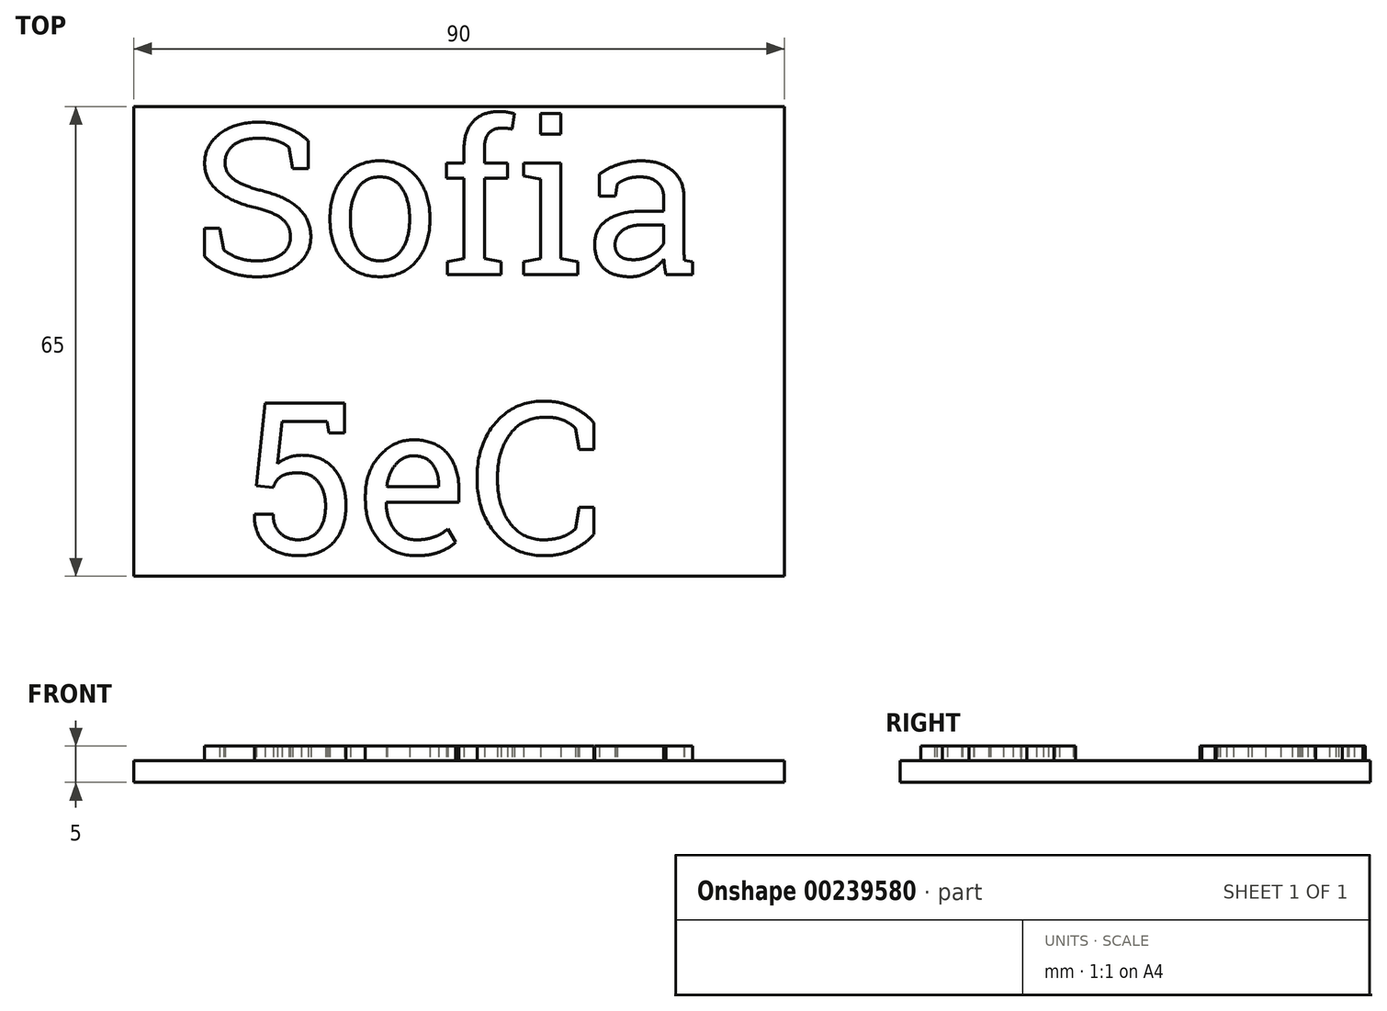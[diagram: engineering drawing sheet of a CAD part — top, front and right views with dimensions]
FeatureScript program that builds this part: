
annotation { "Feature Type Name" : "Feature", "Feature Type Description" : "" }
export const myFeature = defineFeature(function(context is Context, id is Id, definition is map)
    precondition{}
    {
        {
            var Q0;
            Q0=qCreatedBy(makeId("Top.planeOp"),FACE);
            var sketch = newSketch(context, id + "F0", { "sketchPlane" : qUnion([Q0])});
            skLineSegment(sketch, "E0.bottom", {"start": v(0, 0) * mm, "end": v(90, 0) * mm});
            skLineSegment(sketch, "E0.top", {"start": v(0, -65) * mm, "end": v(90, -65) * mm});
            skLineSegment(sketch, "E0.left", {"start": v(0, 0) * mm, "end": v(0, -65) * mm});
            skLineSegment(sketch, "E0.right", {"start": v(90, 0) * mm, "end": v(90, -65) * mm});
            skSolve(sketch);
        }
        {
            var Q0;
            Q0=makeQuery(id+"F0.imprint","IMPRINT",FACE,{"disambiguationData":[TD([[makeQuery(id+"F0.imprint","IMPRINT",EDGE,{"derivedFrom":sQuery(id+"F0.wireOp",EDGE,"E0.bottom")}),-1.0]])]});
            extrude(context, id + "F1", {"entities" : qUnion([Q0]), "depth" : 3 * mm});
        }
        {
            var Q0;
            Q0=makeQuery(id+"F1.opExtrude","CAP_FACE",FACE,{"disambiguationData":[OSD([sQuery(id+"F0.wireOp",EDGE,"E0.bottom"),sQuery(id+"F0.wireOp",EDGE,"E0.top"),sQuery(id+"F0.wireOp",EDGE,"E0.left"),sQuery(id+"F0.wireOp",EDGE,"E0.right")])],"isStart":false});
            var sketch = newSketch(context, id + "F2", { "sketchPlane" : qUnion([Q0])});
            skText(sketch, "E1", { "text": "Sofia \n 5eC", "fontName": "RobotoSlab-Regular.ttf"});
            const initialGuessF2  = {"E1": [0.00807, -0.02326, 1, 0, 0.02105]};
            skSetInitialGuess(sketch, initialGuessF2);
            skSolve(sketch);
        }
        {
            var Q0;
            Q0 = qSketchRegion(id + "F2", true);
            extrude(context, id + "F3", {"entities" : qUnion([Q0]), "operationType" : NewBodyOperationType.ADD, "depth" : 2 * mm});
        }
    });
